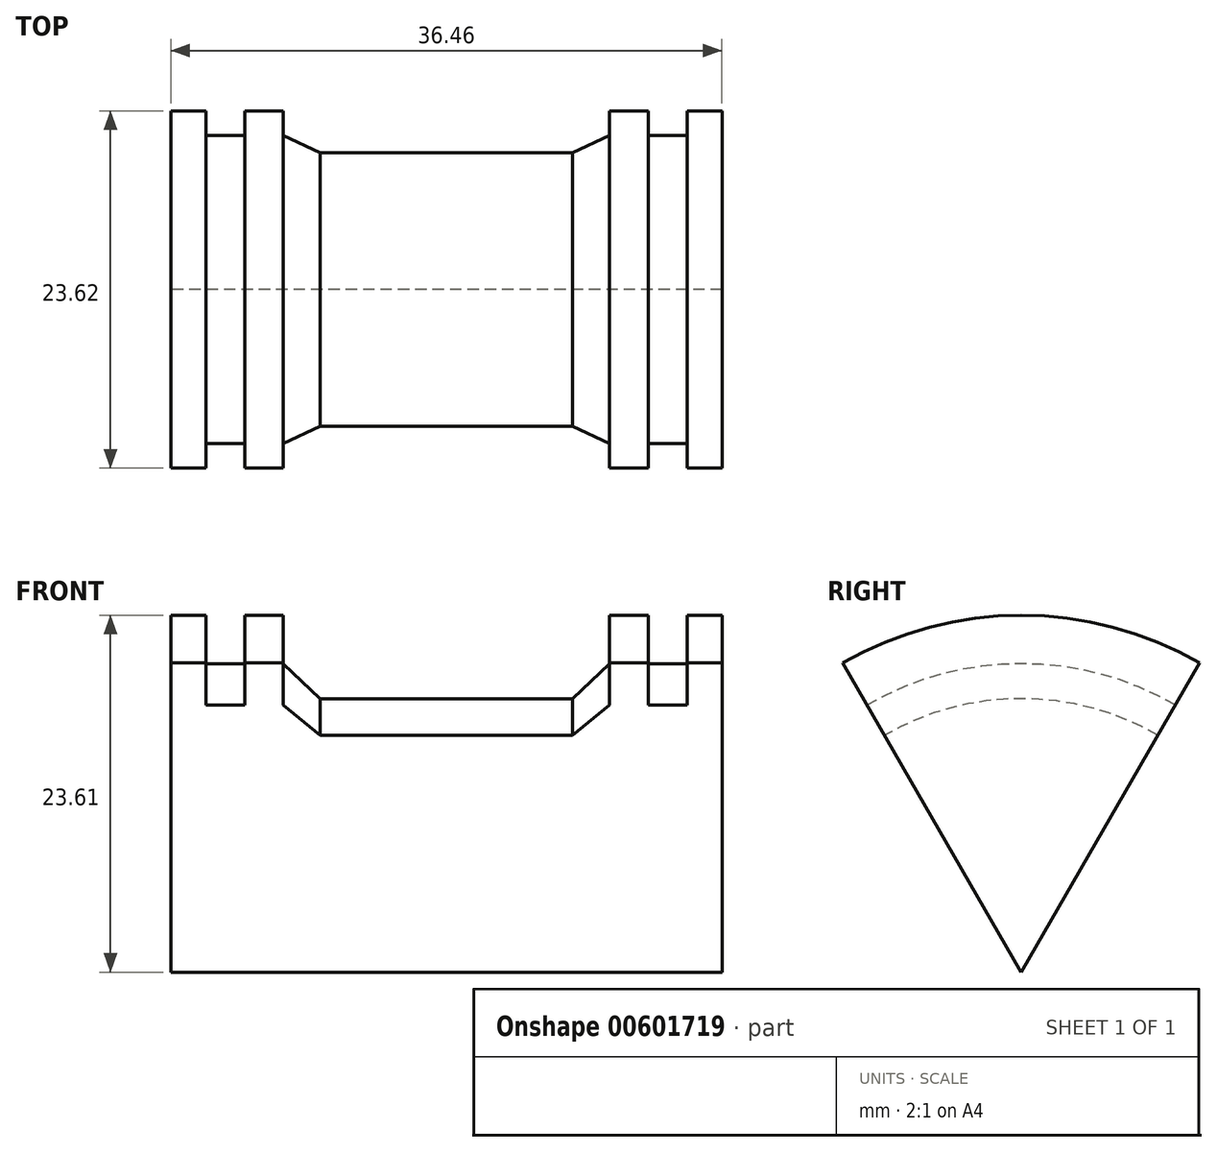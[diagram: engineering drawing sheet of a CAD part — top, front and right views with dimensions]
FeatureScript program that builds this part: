
annotation { "Feature Type Name" : "Feature", "Feature Type Description" : "" }
export const myFeature = defineFeature(function(context is Context, id is Id, definition is map)
    precondition{}
    {
        {
            var Q0;
            Q0=qCreatedBy(makeId("Front.planeOp"),FACE);
            var sketch = newSketch(context, id + "F0", { "sketchPlane" : qUnion([Q0])});
            skLineSegment(sketch, "E0", {"start": v(0, 0) * mm, "end": v(18.23, 0) * mm});
            skLineSegment(sketch, "E1", {"start": v(18.23, 0) * mm, "end": v(18.23, 23.61) * mm});
            skLineSegment(sketch, "E2", {"start": v(18.23, 23.61) * mm, "end": v(15.93, 23.61) * mm});
            skLineSegment(sketch, "E3", {"start": v(15.93, 23.61) * mm, "end": v(15.93, 20.4) * mm});
            skLineSegment(sketch, "E4", {"start": v(15.93, 20.4) * mm, "end": v(13.36, 20.4) * mm});
            skLineSegment(sketch, "E5", {"start": v(13.36, 20.4) * mm, "end": v(13.36, 23.61) * mm});
            skLineSegment(sketch, "E6", {"start": v(13.36, 23.61) * mm, "end": v(10.8, 23.61) * mm});
            skLineSegment(sketch, "E7", {"start": v(10.8, 23.61) * mm, "end": v(10.8, 20.4) * mm});
            skLineSegment(sketch, "E8", {"start": v(10.8, 20.4) * mm, "end": v(8.36, 18.1) * mm});
            skLineSegment(sketch, "E9", {"start": v(8.36, 18.1) * mm, "end": v(0, 18.1) * mm});
            skLineSegment(sketch, "E10", {"start": v(0, 18.1) * mm, "end": v(0, 0) * mm});
            skLineSegment(sketch, "E11.MirrorCS", {"start": v(-18.23, 0) * mm, "end": v(-18.23, 23.61) * mm});
            skLineSegment(sketch, "E12.MirrorCS", {"start": v(-8.36, 18.1) * mm, "end": v(0, 18.1) * mm});
            skLineSegment(sketch, "E13.MirrorCS", {"start": v(-10.8, 20.4) * mm, "end": v(-8.36, 18.1) * mm});
            skLineSegment(sketch, "E14.MirrorCS", {"start": v(-10.8, 23.61) * mm, "end": v(-10.8, 20.4) * mm});
            skLineSegment(sketch, "E15.MirrorCS", {"start": v(-13.36, 23.61) * mm, "end": v(-10.8, 23.61) * mm});
            skLineSegment(sketch, "E16.MirrorCS", {"start": v(-13.36, 20.4) * mm, "end": v(-13.36, 23.61) * mm});
            skLineSegment(sketch, "E17.MirrorCS", {"start": v(-15.93, 20.4) * mm, "end": v(-13.36, 20.4) * mm});
            skLineSegment(sketch, "E18.MirrorCS", {"start": v(-15.93, 23.61) * mm, "end": v(-15.93, 20.4) * mm});
            skLineSegment(sketch, "E19.MirrorCS", {"start": v(-18.23, 23.61) * mm, "end": v(-15.93, 23.61) * mm});
            skLineSegment(sketch, "E20.MirrorCS", {"start": v(0, 0) * mm, "end": v(-18.23, 0) * mm});
            skSolve(sketch);
        }
        {
            var Q0;
            Q0=makeQuery(id+"F0.imprint","IMPRINT",FACE,{"disambiguationData":[TD([[makeQuery(id+"F0.imprint","IMPRINT",EDGE,{"derivedFrom":sQuery(id+"F0.wireOp",EDGE,"E10")}),-1.0]])]});
            var Q1;
            Q1=makeQuery(id+"F0.imprint","IMPRINT",FACE,{"disambiguationData":[TD([[makeQuery(id+"F0.imprint","IMPRINT",EDGE,{"derivedFrom":sQuery(id+"F0.wireOp",EDGE,"E0")}),1.0]])]});
            var Q2;
            Q2=sQuery(id+"F0.wireOp",EDGE,"E0");
            revolve(context, id + "F1", {"entities" : qUnion([Q0, Q1]), "axis" : qUnion([Q2]), "revolveType" : RevolveType.TWO_DIRECTIONS, "angle" : 30 * degree, "angleBack" : 330 * degree});
        }
    });
